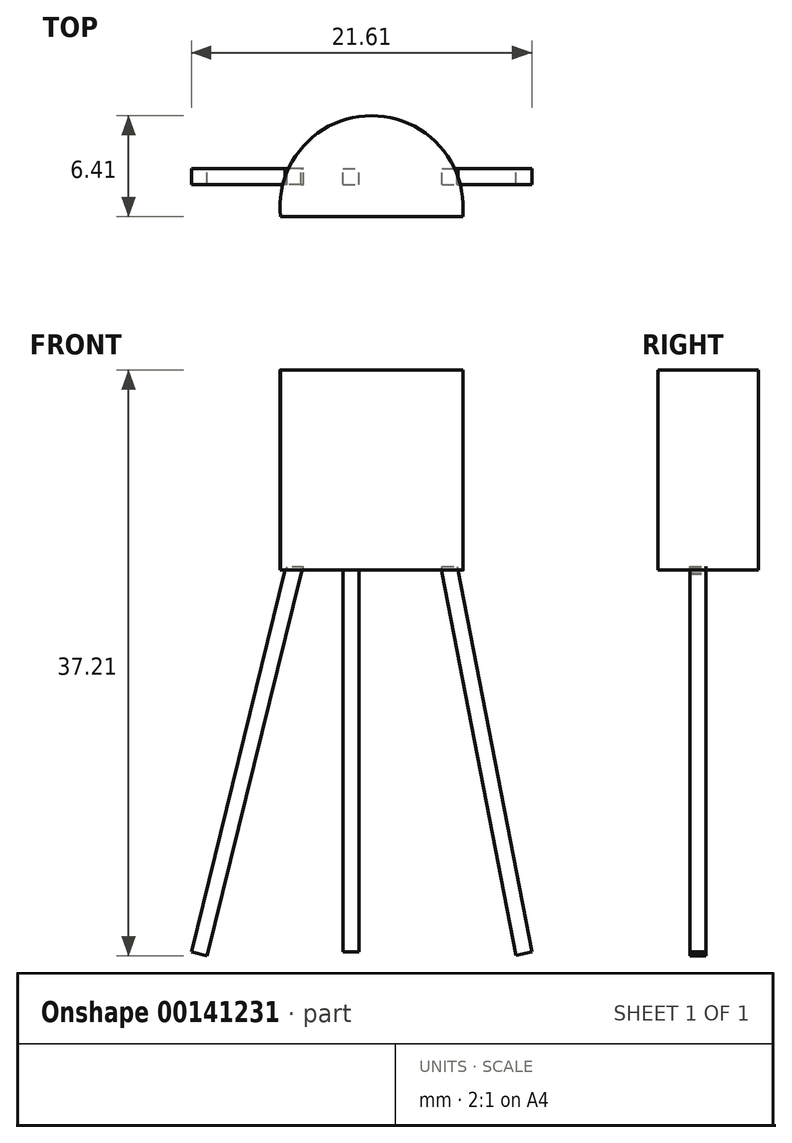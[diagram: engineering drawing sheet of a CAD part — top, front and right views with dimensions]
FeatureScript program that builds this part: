
annotation { "Feature Type Name" : "Feature", "Feature Type Description" : "" }
export const myFeature = defineFeature(function(context is Context, id is Id, definition is map)
    precondition{}
    {
        {
            var Q0;
            Q0=qCreatedBy(makeId("Top.planeOp"),FACE);
            var sketch = newSketch(context, id + "F0", { "sketchPlane" : qUnion([Q0])});
            skArc(sketch, "E0", {"start": v(6.58, 0) * mm, "mid": v(0.78, 6.4) * mm, "end": v(-5.01, 0) * mm});
            skLineSegment(sketch, "E1", {"start": v(-5.01, 0) * mm, "end": v(6.58, 0) * mm});
            skSolve(sketch);
        }
        {
            var Q0;
            Q0 = qSketchRegion(id + "F0", true);
            extrude(context, id + "F1", {"entities" : qUnion([Q0]), "depth" : 12.7 * mm});
        }
        {
            var Q0;
            Q0=qCreatedBy(makeId("Front.planeOp"),FACE);
            cPlane(context, id + "F2", {"entities" : qUnion([Q0]), "cplaneType" : CPlaneType.OFFSET, "offset" : 3.05 * mm, "oppositeDirection" : true, "width" : 152.4 * mm, "height" : 152.4 * mm});
        }
        {
            var Q0;
            Q0=qCreatedBy(id+"F2.planeOp",FACE);
            var sketch = newSketch(context, id + "F3", { "sketchPlane" : qUnion([Q0])});
            skLineSegment(sketch, "E2", {"start": v(6.26, 0) * mm, "end": v(10.96, -24.27) * mm});
            skLineSegment(sketch, "E3", {"start": v(0, 0) * mm, "end": v(0, -24.27) * mm});
            skLineSegment(sketch, "E4", {"start": v(-4.7, 0) * mm, "end": v(-10.65, -24.27) * mm});
            skLineSegment(sketch, "E5.0", {"start": v(-3.71, -0.24) * mm, "end": v(-9.66, -24.51) * mm});
            skLineSegment(sketch, "E6.0", {"start": v(-1.02, 0) * mm, "end": v(-1.02, -24.27) * mm});
            skLineSegment(sketch, "E7.0", {"start": v(5.27, -0.2) * mm, "end": v(9.96, -24.46) * mm});
            skLineSegment(sketch, "E8", {"start": v(-3.71, -0.24) * mm, "end": v(-3.53, 0.2) * mm});
            skLineSegment(sketch, "E9", {"start": v(-3.53, 0.2) * mm, "end": v(-4.6, 0.2) * mm});
            skLineSegment(sketch, "E10", {"start": v(-4.6, 0.2) * mm, "end": v(-4.7, 0) * mm});
            skLineSegment(sketch, "E11", {"start": v(5.27, -0.2) * mm, "end": v(5.27, 0.22) * mm});
            skLineSegment(sketch, "E12", {"start": v(5.27, 0.22) * mm, "end": v(6.2, 0.22) * mm});
            skLineSegment(sketch, "E13", {"start": v(6.2, 0.22) * mm, "end": v(6.26, 0) * mm});
            skLineSegment(sketch, "E14", {"start": v(9.96, -24.46) * mm, "end": v(10.96, -24.27) * mm});
            skLineSegment(sketch, "E15", {"start": v(-1.02, -24.27) * mm, "end": v(0, -24.27) * mm});
            skLineSegment(sketch, "E16", {"start": v(-10.65, -24.27) * mm, "end": v(-9.66, -24.51) * mm});
            skLineSegment(sketch, "E17", {"start": v(-1.02, 0) * mm, "end": v(0, 0) * mm});
            skSolve(sketch);
        }
        {
            var Q0;
            Q0 = qSketchRegion(id + "F3", true);
            extrude(context, id + "F4", {"entities" : qUnion([Q0]), "depth" : 1.02 * mm});
        }
    });
